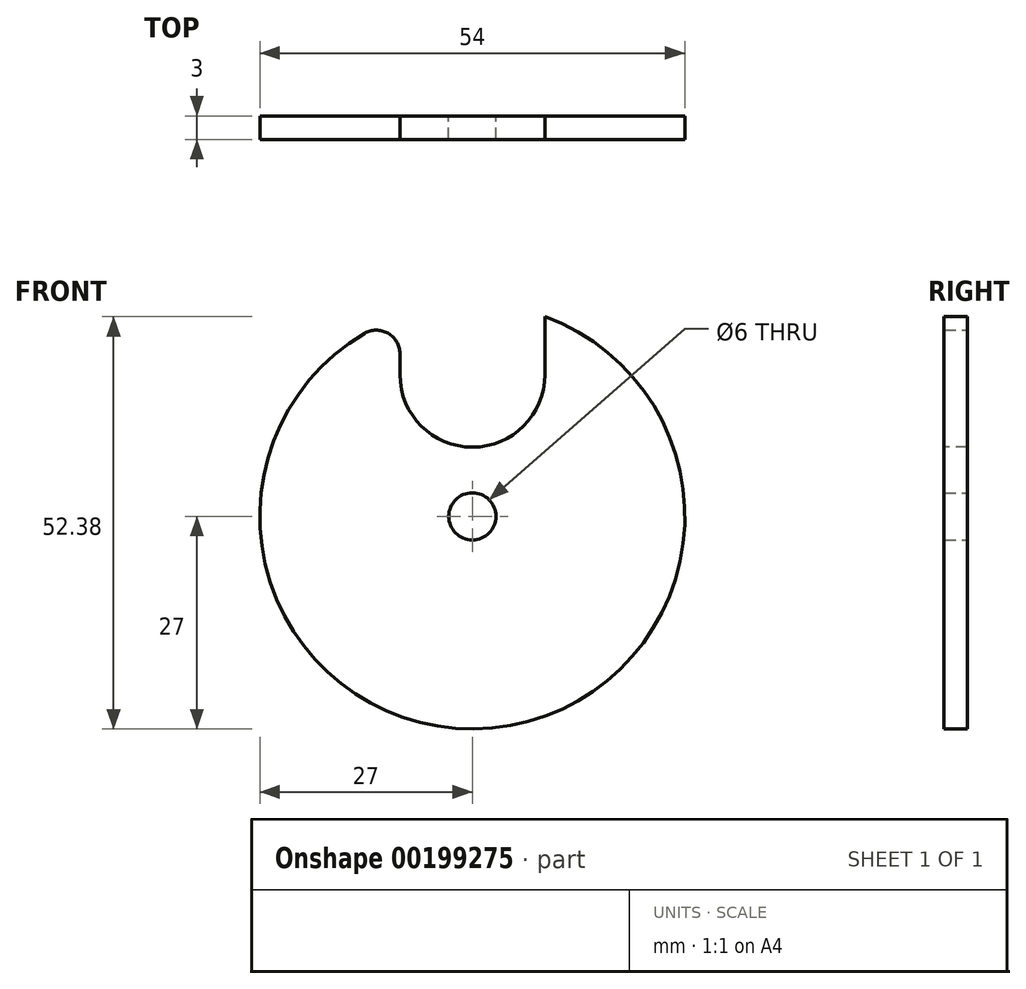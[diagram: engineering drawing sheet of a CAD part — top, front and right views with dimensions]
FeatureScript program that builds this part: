
annotation { "Feature Type Name" : "Feature", "Feature Type Description" : "" }
export const myFeature = defineFeature(function(context is Context, id is Id, definition is map)
    precondition{}
    {
        {
            var Q0;
            Q0=qCreatedBy(makeId("Front.planeOp"),FACE);
            var sketch = newSketch(context, id + "F0", { "sketchPlane" : qUnion([Q0])});
            skCircle(sketch, "E0", {"center": v(0, 0) * mm, "radius": 27 * mm});
            skCircle(sketch, "E1", {"center": v(0, 0) * mm, "radius": 3 * mm});
            skSolve(sketch);
        }
        {
            var Q0;
            Q0 = qSketchRegion(id + "F0", true);
            extrude(context, id + "F1", {"entities" : qUnion([Q0]), "depth" : 3 * mm});
        }
        {
            var Q0;
            Q0=makeQuery(id+"F1.opExtrude","CAP_FACE",FACE,{"disambiguationData":[OSD([sQuery(id+"F0.wireOp",EDGE,"E0"),sQuery(id+"F0.wireOp",EDGE,"E1")])],"isStart":false});
            var sketch = newSketch(context, id + "F2", { "sketchPlane" : qUnion([Q0])});
            skArc(sketch, "E2", {"start": v(-9.2, 18) * mm, "mid": v(0, 8.8) * mm, "end": v(9.2, 18) * mm});
            skLineSegment(sketch, "E3", {"start": v(-9.2, 18) * mm, "end": v(-9.2, 30.6) * mm});
            skLineSegment(sketch, "E4", {"start": v(-9.2, 30.6) * mm, "end": v(9.2, 30.6) * mm});
            skLineSegment(sketch, "E5", {"start": v(9.2, 30.6) * mm, "end": v(9.2, 18) * mm});
            skSolve(sketch);
        }
        {
            var Q0;
            Q0 = qSketchRegion(id + "F2", true);
            extrude(context, id + "F3", {"entities" : qUnion([Q0]), "operationType" : NewBodyOperationType.REMOVE, "oppositeDirection" : true, "depth" : 3 * mm});
        }
        {
            var Q0;
            Q0=makeQuery(id+"F3.boolean.opBoolean","INTERSECT",EDGE,{"derivedFrom":[makeQuery(id+"F1.opExtrude","SWEPT_FACE",FACE,{"disambiguationData":[OSD([sQuery(id+"F0.wireOp",EDGE,"E0")])]}),makeQuery(id+"F3.opExtrude","SWEPT_FACE",FACE,{"disambiguationData":[OSD([sQuery(id+"F2.wireOp",EDGE,"bzEhMXPJ-w0G5-mEWT-vxi7-O08ZO4qL7Rpj")])]})]});
            var Q1;
            Q1=makeQuery(id+"F3.boolean.opBoolean","INTERSECT",EDGE,{"derivedFrom":[makeQuery(id+"F1.opExtrude","SWEPT_FACE",FACE,{"disambiguationData":[OSD([sQuery(id+"F0.wireOp",EDGE,"E0")])]}),makeQuery(id+"F3.opExtrude","SWEPT_FACE",FACE,{"disambiguationData":[OSD([sQuery(id+"F2.wireOp",EDGE,"E3")])]})]});
            fillet(context, id + "F4", {"entities" : qUnion([Q0, Q1]), "radius" : 3 * mm, "tangentPropagation" : true, "allowEdgeOverflow" : false});
        }
    });
